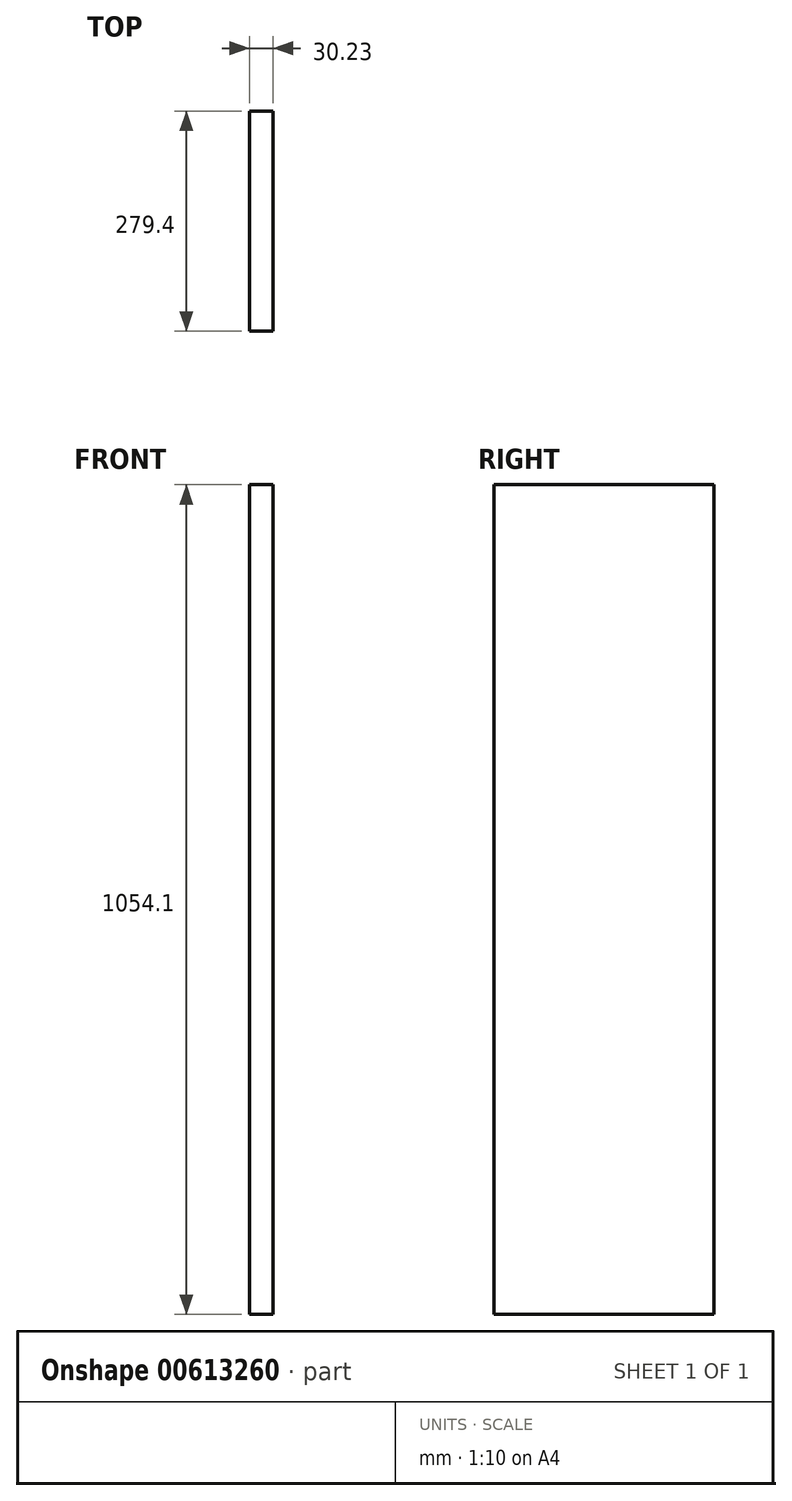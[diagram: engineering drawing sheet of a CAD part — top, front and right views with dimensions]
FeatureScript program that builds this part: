
annotation { "Feature Type Name" : "Feature", "Feature Type Description" : "" }
export const myFeature = defineFeature(function(context is Context, id is Id, definition is map)
    precondition{}
    {
        {
            var Q0;
            Q0=qCreatedBy(makeId("Right.planeOp"),FACE);
            var sketch = newSketch(context, id + "F0", { "sketchPlane" : qUnion([Q0])});
            skLineSegment(sketch, "E0.bottom", {"start": v(139.7, 527.05) * mm, "end": v(-139.7, 527.05) * mm});
            skLineSegment(sketch, "E0.top", {"start": v(139.7, -527.05) * mm, "end": v(-139.7, -527.05) * mm});
            skLineSegment(sketch, "E0.left", {"start": v(139.7, 527.05) * mm, "end": v(139.7, -527.05) * mm});
            skLineSegment(sketch, "E0.right", {"start": v(-139.7, 527.05) * mm, "end": v(-139.7, -527.05) * mm});
            skPoint(sketch, "E0.middle", {"position": v(0, 0) * mm});
            skSolve(sketch);
        }
        {
            var Q0;
            Q0=makeQuery(id+"F0.imprint","IMPRINT",FACE,{"disambiguationData":[TD([[makeQuery(id+"F0.imprint","IMPRINT",EDGE,{"derivedFrom":sQuery(id+"F0.wireOp",EDGE,"E0.bottom")}),1.0]])]});
            extrude(context, id + "F1", {"entities" : qUnion([Q0]), "depth" : 30.23 * mm, "offsetDistance" : 25.4 * mm});
        }
    });
